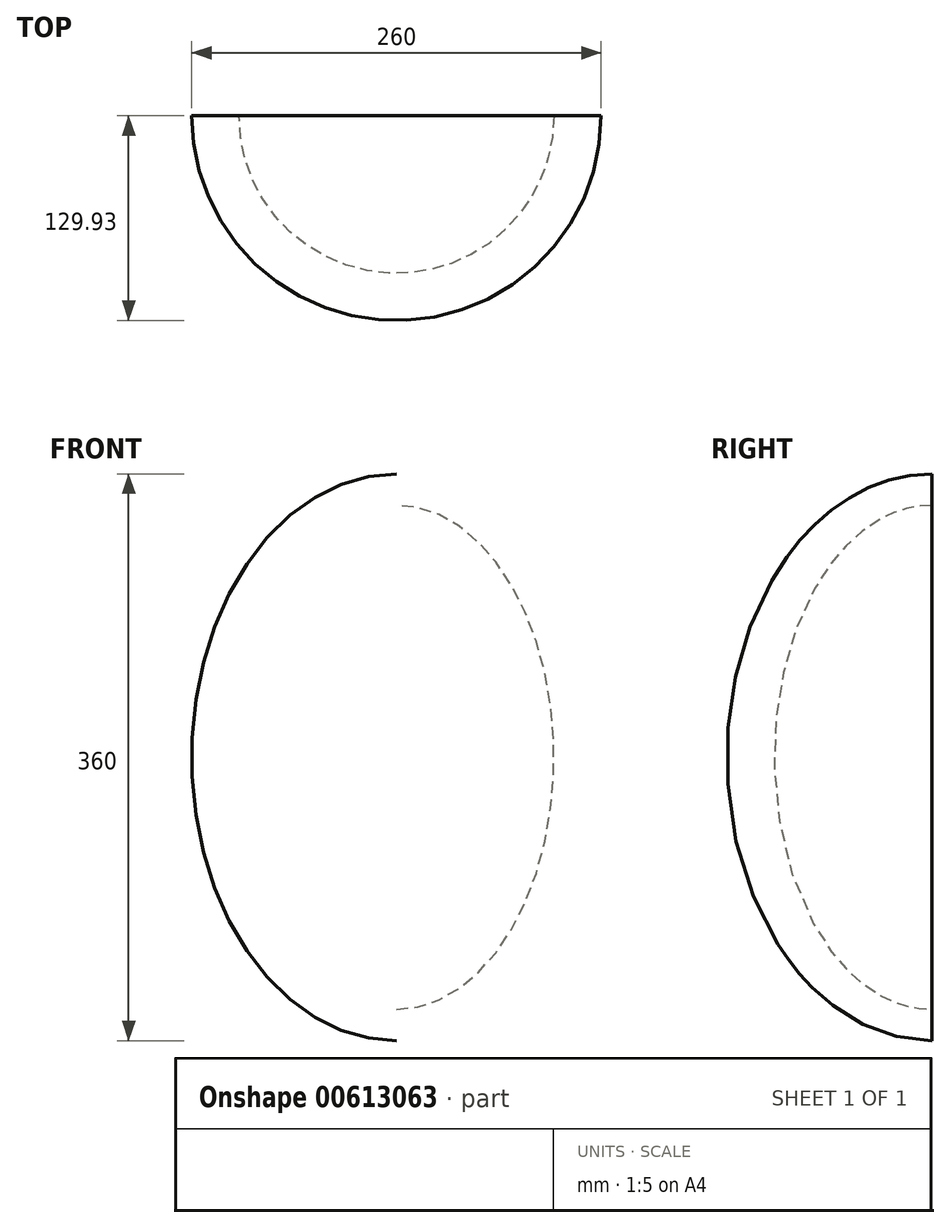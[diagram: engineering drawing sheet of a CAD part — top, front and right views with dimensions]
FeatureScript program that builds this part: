
annotation { "Feature Type Name" : "Feature", "Feature Type Description" : "" }
export const myFeature = defineFeature(function(context is Context, id is Id, definition is map)
    precondition{}
    {
        {
            var Q0;
            Q0=qCreatedBy(makeId("Front.planeOp"),FACE);
            var sketch = newSketch(context, id + "F0", { "sketchPlane" : qUnion([Q0])});
            skEllipticalArc(sketch, "E0", {});
            skEllipticalArc(sketch, "E1", {});
            skLineSegment(sketch, "E2", {"start": v(0, 180) * mm, "end": v(0, 160) * mm});
            skLineSegment(sketch, "E3", {"start": v(0, -160) * mm, "end": v(0, -180) * mm});
            const initialGuessF0  = {"E0": [0, 0, 0, -1, 0.18, 0.13, 0, 3.141592653589793], "E1": [0, 0, 1, 0, 0.1, 0.16, 4.71238898038469, 1.5707963267948966]};
            skSetInitialGuess(sketch, initialGuessF0);
            skSolve(sketch);
        }
        {
            var Q0;
            Q0=makeQuery(id+"F0.imprint","IMPRINT",FACE,{"disambiguationData":[TD([[makeQuery(id+"F0.imprint","IMPRINT",EDGE,{"derivedFrom":sQuery(id+"F0.wireOp",EDGE,"E0")}),1.0]])]});
            var Q1;
            Q1=sQuery(id+"F0.wireOp",EDGE,"E2");
            revolve(context, id + "F1", {"entities" : qUnion([Q0]), "axis" : qUnion([Q1]), "revolveType" : RevolveType.ONE_DIRECTION, "angle" : 180 * degree});
        }
    });
